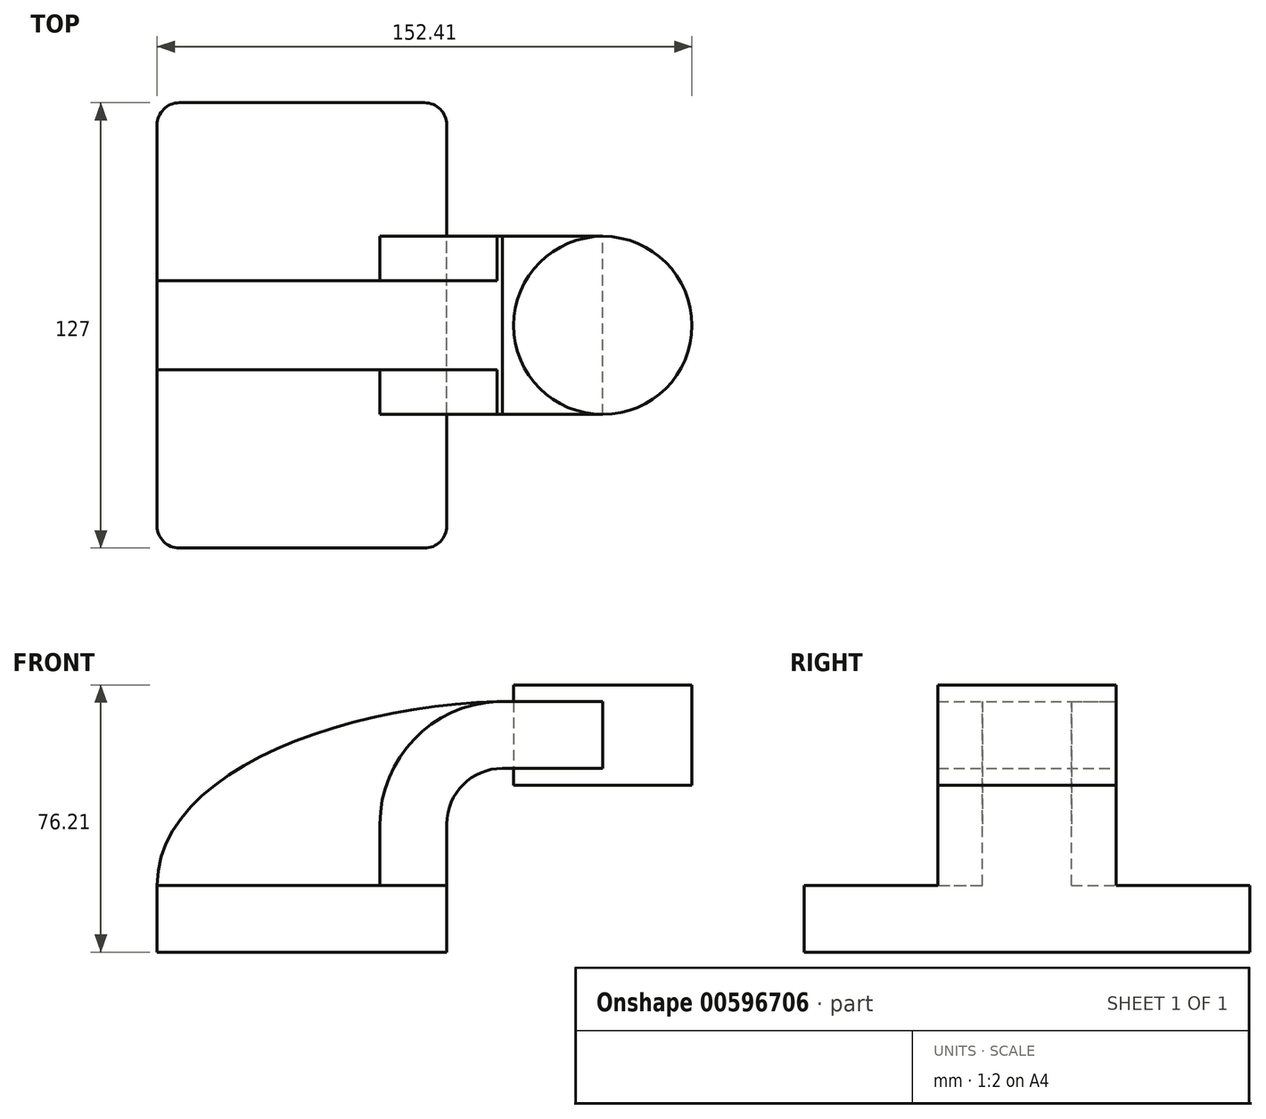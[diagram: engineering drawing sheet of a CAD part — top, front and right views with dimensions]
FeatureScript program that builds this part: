
annotation { "Feature Type Name" : "Feature", "Feature Type Description" : "" }
export const myFeature = defineFeature(function(context is Context, id is Id, definition is map)
    precondition{}
    {
        {
            var Q0;
            Q0=qCreatedBy(makeId("Front.planeOp"),FACE);
            var sketch = newSketch(context, id + "F0", { "sketchPlane" : qUnion([Q0])});
            skLineSegment(sketch, "E0.bottom", {"start": v(-41.27, -9.53) * mm, "end": v(41.28, -9.53) * mm});
            skLineSegment(sketch, "E0.top", {"start": v(-41.28, 9.53) * mm, "end": v(41.28, 9.53) * mm});
            skLineSegment(sketch, "E0.left", {"start": v(-41.28, -9.53) * mm, "end": v(-41.28, 9.53) * mm});
            skLineSegment(sketch, "E0.right", {"start": v(41.28, -9.53) * mm, "end": v(41.28, 9.52) * mm});
            skPoint(sketch, "E0.middle", {"position": v(0, 0) * mm});
            skLineSegment(sketch, "E1.bottom", {"start": v(60.32, 66.67) * mm, "end": v(111.12, 66.67) * mm});
            skLineSegment(sketch, "E1.top", {"start": v(60.32, 38.1) * mm, "end": v(111.12, 38.1) * mm});
            skLineSegment(sketch, "E1.left", {"start": v(60.32, 66.67) * mm, "end": v(60.32, 38.1) * mm});
            skLineSegment(sketch, "E1.right", {"start": v(111.12, 66.67) * mm, "end": v(111.12, 38.1) * mm});
            skPoint(sketch, "E1.middle", {"position": v(85.72, 52.39) * mm});
            skLineSegment(sketch, "E2", {"start": v(41.28, 9.52) * mm, "end": v(41.28, 27) * mm});
            skArc(sketch, "E3", {"start": v(41.27, 27) * mm, "mid": v(45.92, 38.23) * mm, "end": v(57.15, 42.88) * mm});
            skLineSegment(sketch, "E4", {"start": v(57.15, 42.88) * mm, "end": v(85.72, 42.88) * mm});
            skLineSegment(sketch, "E5.0", {"start": v(57.15, 61.93) * mm, "end": v(85.72, 61.93) * mm});
            skArc(sketch, "E5.1", {"start": v(22.23, 27) * mm, "mid": v(32.45, 51.7) * mm, "end": v(57.15, 61.93) * mm});
            skLineSegment(sketch, "E5.2", {"start": v(22.22, 9.52) * mm, "end": v(22.22, 27) * mm});
            skFitSpline(sketch, "E6", {"points": [v(-41.28, 9.53) * mm, v(57.15, 61.93) * mm], "startDerivative": vector(0.3, 97.47) * mm, "endDerivative": vector(135.62, 2.4) * mm});
            skLineSegment(sketch, "E7", {"start": v(85.72, 38.1) * mm, "end": v(85.72, 66.67) * mm});
            skSolve(sketch);
        }
        {
            var Q0;
            Q0=makeQuery(id+"F0.imprint","IMPRINT",FACE,{"disambiguationData":[TD([[makeQuery(id+"F0.imprint","IMPRINT",EDGE,{"derivedFrom":sQuery(id+"F0.wireOp",EDGE,"E0.bottom")}),1.0]])]});
            extrude(context, id + "F1", {"entities" : qUnion([Q0]), "endBound" : BoundingType.SYMMETRIC, "depth" : 127 * mm, "offsetDistance" : 25.4 * mm});
        }
        {
            var Q0;
            {var subQ0=sQuery(id+"F0.wireOp",EDGE,"E2");Q0=makeQuery(id+"F0.imprint","IMPRINT",FACE,{"disambiguationData":[TD([[makeQuery(id+"F0.imprint","IMPRINT",EDGE,{"derivedFrom":subQ0}),1.0]])]});}
            var Q1;
            {var subQ5=sQuery(id+"F0.wireOp",EDGE,"ATxHrx0p-2Vgf-qdOY-SYWu-a5K56bYOCua9");Q1=makeQuery(id+"F0.imprint","IMPRINT",FACE,{"disambiguationData":[TD([[makeQuery(id+"F0.imprint","IMPRINT",EDGE,{"derivedFrom":subQ5}),1.0]])]});}
            var Q2;
            {var subQ0=sQuery(id+"F0.wireOp",EDGE,"E5.0");var subQ1=sQuery(id+"F0.wireOp",EDGE,"E1.left");var subQ2=makeQuery(id+"F0.imprint","INTERSECT",VERTEX,{"derivedFrom":[subQ1,subQ0]});Q2=makeQuery(id+"F0.imprint","IMPRINT",FACE,{"disambiguationData":[TD([[makeQuery(id+"F0.imprint","IMPRINT",EDGE,{"disambiguationData":[TD([[subQ2,-1.0]])],"derivedFrom":subQ1}),1.0]])]});}
            extrude(context, id + "F2", {"entities" : qUnion([Q0, Q1, Q2]), "operationType" : NewBodyOperationType.ADD, "endBound" : BoundingType.SYMMETRIC, "depth" : 50.8 * mm, "offsetDistance" : 25.4 * mm});
        }
        {
            var Q0;
            {var subQ3=sQuery(id+"F0.wireOp",EDGE,"E5.2");Q0=makeQuery(id+"F0.imprint","IMPRINT",FACE,{"disambiguationData":[TD([[makeQuery(id+"F0.imprint","IMPRINT",EDGE,{"derivedFrom":subQ3}),1.0]])]});}
            extrude(context, id + "F3", {"entities" : qUnion([Q0]), "operationType" : NewBodyOperationType.ADD, "endBound" : BoundingType.SYMMETRIC, "depth" : 25.4 * mm, "offsetDistance" : 25.4 * mm});
        }
        {
            var Q0;
            {var subQ4=sQuery(id+"F0.wireOp",EDGE,"E1.right");Q0=makeQuery(id+"F0.imprint","IMPRINT",FACE,{"disambiguationData":[TD([[makeQuery(id+"F0.imprint","IMPRINT",EDGE,{"derivedFrom":subQ4}),-1.0]])]});}
            var Q1;
            Q1=sQuery(id+"F0.wireOp",EDGE,"E7");
            revolve(context, id + "F4", {"entities" : qUnion([Q0]), "axis" : qUnion([Q1]), "revolveType" : RevolveType.FULL});
        }
        {
            var Q0;
            Q0=makeQuery(id+"F1.opExtrude","CAP_EDGE",EDGE,{"disambiguationData":[OSD([sQuery(id+"F0.wireOp",EDGE,"E0.right")])],"isStart":false});
            var Q1;
            Q1=makeQuery(id+"F1.opExtrude","CAP_EDGE",EDGE,{"disambiguationData":[OSD([sQuery(id+"F0.wireOp",EDGE,"E0.right")])],"isStart":true});
            var Q2;
            Q2=makeQuery(id+"F1.opExtrude","CAP_EDGE",EDGE,{"disambiguationData":[OSD([sQuery(id+"F0.wireOp",EDGE,"E0.left")])],"isStart":false});
            var Q3;
            Q3=makeQuery(id+"F1.opExtrude","CAP_EDGE",EDGE,{"disambiguationData":[OSD([sQuery(id+"F0.wireOp",EDGE,"E0.left")])],"isStart":true});
            fillet(context, id + "F5", {"entities" : qUnion([Q0, Q1, Q2, Q3]), "radius" : 6.35 * mm, "tangentPropagation" : true, "allowEdgeOverflow" : false});
        }
    });
